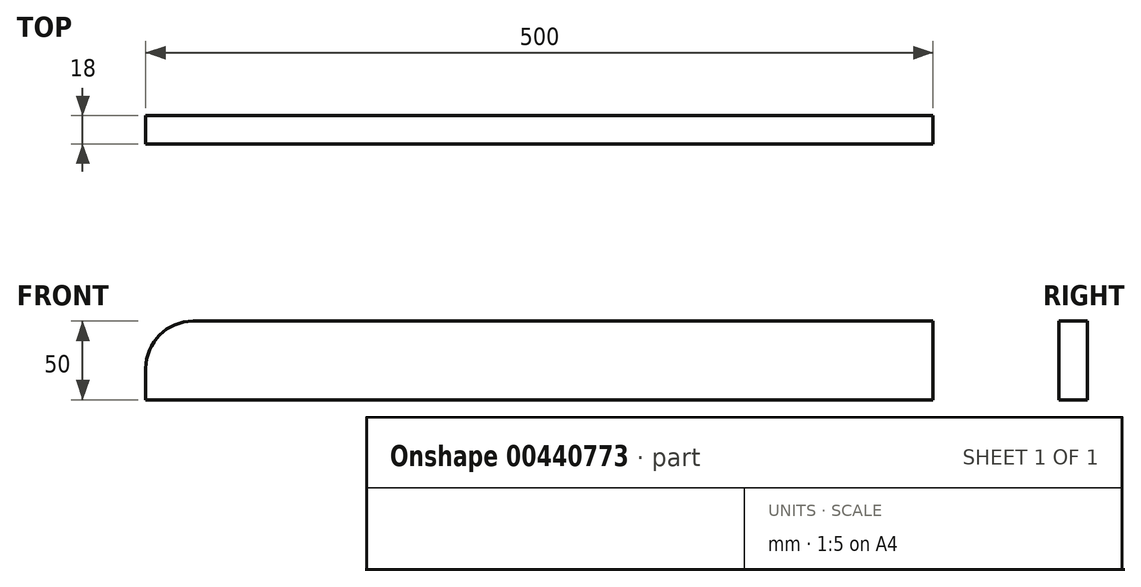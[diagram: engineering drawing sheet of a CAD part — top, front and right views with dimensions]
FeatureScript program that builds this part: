
annotation { "Feature Type Name" : "Feature", "Feature Type Description" : "" }
export const myFeature = defineFeature(function(context is Context, id is Id, definition is map)
    precondition{}
    {
        {
            var Q0;
            Q0=qCreatedBy(makeId("Front.planeOp"),FACE);
            var sketch = newSketch(context, id + "F0", { "sketchPlane" : qUnion([Q0])});
            skLineSegment(sketch, "E0.bottom", {"start": v(-470, 50) * mm, "end": v(0, 50) * mm});
            skLineSegment(sketch, "E0.top", {"start": v(-500, 0) * mm, "end": v(0, 0) * mm});
            skLineSegment(sketch, "E0.left", {"start": v(-500, 20) * mm, "end": v(-500, 0) * mm});
            skLineSegment(sketch, "E0.right", {"start": v(0, 50) * mm, "end": v(0, 0) * mm});
            skPoint(sketch, "E1.visualSharp", {"position": v(-500, 50) * mm});
            skArc(sketch, "E1.filletArc", {"start": v(-470, 50) * mm, "mid": v(-491.21, 41.21) * mm, "end": v(-500, 20) * mm});
            skSolve(sketch);
        }
        {
            var Q0;
            Q0 = qSketchRegion(id + "F0", true);
            extrude(context, id + "F1", {"entities" : qUnion([Q0]), "depth" : 18 * mm});
        }
    });
